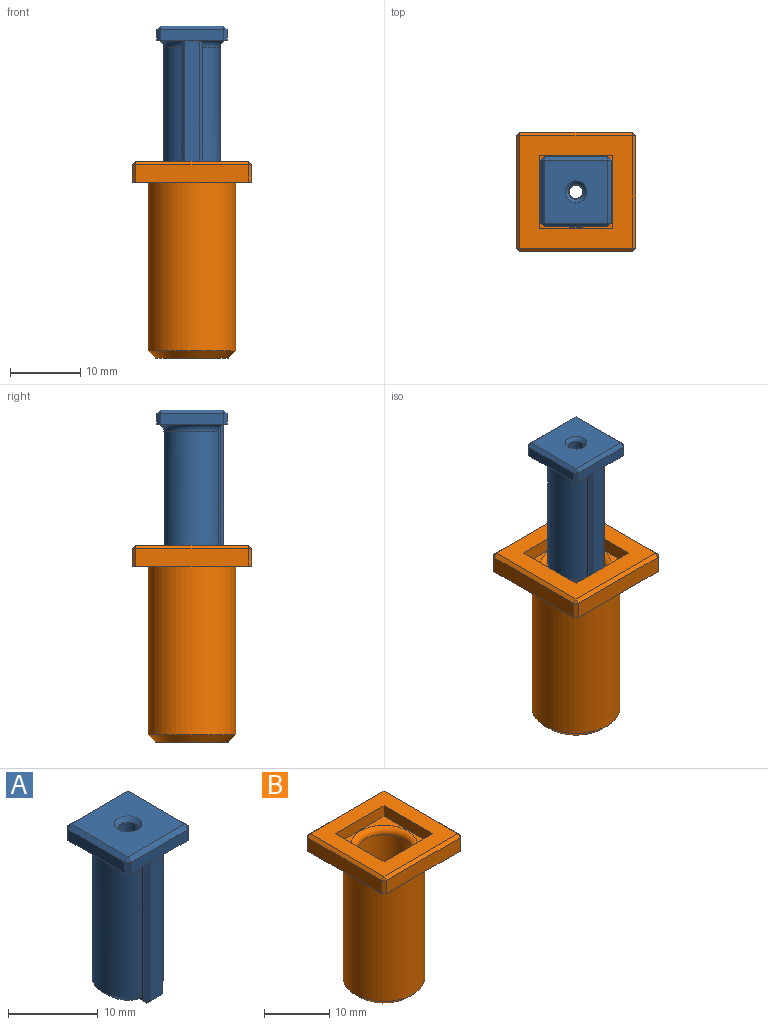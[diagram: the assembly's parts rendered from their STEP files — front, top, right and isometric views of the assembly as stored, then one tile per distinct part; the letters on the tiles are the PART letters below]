
ASSEMBLY  parts=2 mates=1
PART A: 39 faces, bbox 10.9x10.9x22 mm
  f0: plane 5x5mm, normal (0,0,-1), area 5.2mm2, adj f4,f7,f24,f30
  f1: plane 5x5mm, normal (0,0,-1), area 5.2mm2, adj f4,f5,f23,f30
  f2: plane 5x5mm, normal (0,0,-1), area 5.2mm2, adj f5,f6,f17,f30
  f3: plane 5x5mm, normal (0,0,-1), area 5.2mm2, adj f6,f7,f18,f30
  f4: plane 9x1.5mm, normal (1,0,0), area 13.5mm2, adj f0,f1,f23,f24,f28
  f5: plane 9x1.5mm, normal (0,1,0), area 13.5mm2, adj f1,f2,f17,f22,f23
  f6: plane 9x1.5mm, normal (-1,0,0), area 13.5mm2, adj f2,f3,f17,f18,f19
  f7: plane 9x1.5mm, normal (0,-1,0), area 13.5mm2, adj f0,f3,f18,f24,f25
  f8: plane 9x9mm, normal (0,0,1), area 73.5mm2, adj f19,f22,f25,f28,f29
  f9: cylinder r=4mm len=18mm, axis (0,0,1), area 397mm2, adj f10,f12,f30,f31
  f10: plane 19.23x0.89mm, normal (1,0,0), area 5.7mm2, adj f9,f30,f31,f35,f38
  f11: plane 19.42x2mm, normal (0,-1,0), area 38.8mm2, adj f30,f33,f36,f38
  f12: plane 19.23x0.89mm, normal (-1,0,0), area 5.7mm2, adj f9,f30,f31,f32,f33
  f13: plane 7x6mm, normal (0,0,-1), area 27.6mm2, adj f14,f31,f32,f35,f36
  f14: cylinder r=0.95mm len=7mm, axis (0,0,1), area 41.8mm2, adj f13,f16
  f15: cylinder r=1.05mm len=14.5mm, axis (0,0,1), area 95.7mm2, adj f16,f29
  f16: plane 2.1x2.1mm, normal (0,0,1), area 0.6mm2, adj f14,f15
  f17: plane 1.5x0.5mm, normal (-0.71,0.71,0), area 1.1mm2, adj f2,f5,f6,f20
  f18: plane 1.5x0.5mm, normal (-0.71,-0.71,0), area 1.1mm2, adj f3,f6,f7,f21
  f19: plane 9x0.5mm, normal (-0.71,0,0.71), area 6.4mm2, adj f6,f8,f20,f21
  f20: plane 0.5x0.5mm, normal (-0.58,0.58,0.58), area 0.2mm2, adj f17,f19,f22
  f21: plane 0.5x0.5mm, normal (-0.58,-0.58,0.58), area 0.2mm2, adj f18,f19,f25
  f22: plane 9x0.5mm, normal (0,0.71,0.71), area 6.4mm2, adj f5,f8,f20,f26
  f23: plane 1.5x0.5mm, normal (0.71,0.71,0), area 1.1mm2, adj f1,f4,f5,f26
  f24: plane 1.5x0.5mm, normal (0.71,-0.71,0), area 1.1mm2, adj f0,f4,f7,f27
  f25: plane 9x0.5mm, normal (0,-0.71,0.71), area 6.4mm2, adj f7,f8,f21,f27
  f26: plane 0.5x0.5mm, normal (0.58,0.58,0.58), area 0.2mm2, adj f22,f23,f28
  f27: plane 0.5x0.5mm, normal (0.58,-0.58,0.58), area 0.2mm2, adj f24,f25,f28
  f28: plane 9x0.5mm, normal (0.71,0,0.71), area 6.4mm2, adj f4,f8,f26,f27
  f29: cone r=1.05mm half-angle=45deg, axis (0,0,1), area 5.8mm2, adj f8,f15
  f30: torus R=5mm, axis (0,0,1), area 39.9mm2, adj f0,f1,f2,f3,f9,f10,f11,f12
  f31: cone r=3mm half-angle=45deg, axis (0,0,1), area 27.1mm2, adj f9,f10,f12,f13,f32,f35
  f32: plane 1.19x0.52mm, normal (-0.71,0,-0.71), area 0.7mm2, adj f12,f13,f31,f34
  f33: plane 19.44x0.51mm, normal (-0.71,-0.71,0), area 13.7mm2, adj f11,f12,f30,f34
  f34: plane 0.5x0.5mm, normal (-0.58,-0.58,-0.58), area 0.2mm2, adj f32,f33,f36
  f35: plane 1.19x0.52mm, normal (0.71,0,-0.71), area 0.7mm2, adj f10,f13,f31,f37
  f36: plane 2x0.5mm, normal (0,-0.71,-0.71), area 1.4mm2, adj f11,f13,f34,f37
  f37: plane 0.5x0.5mm, normal (0.58,-0.58,-0.58), area 0.2mm2, adj f35,f36,f38
  f38: plane 19.44x0.51mm, normal (0.71,-0.71,0), area 13.7mm2, adj f10,f11,f30,f37
PART B: 38 faces, bbox 21x21x32 mm
  f0: torus R=5.05mm, axis (0,0,1), area 199.4mm2, adj f13,f16
  f1: plane 16x16mm, normal (0,0,1), area 145.7mm2, adj f9,f10,f11,f12,f27,f30,f33,f36
  f2: plane 16x2.5mm, normal (0,-1,0), area 40mm2, adj f6,f25,f30,f31
  f3: plane 16x2.5mm, normal (1,0,0), area 40mm2, adj f6,f25,f26,f27
  f4: plane 16x2.5mm, normal (0,1,0), area 40mm2, adj f6,f26,f32,f33
  f5: plane 16x2.5mm, normal (-1,0,0), area 40mm2, adj f6,f31,f32,f36
  f6: plane 17x17mm, normal (0,0,-1), area 165.8mm2, adj f2,f3,f4,f5,f7,f25,f26,f31
  f7: cylinder r=6.25mm len=24mm, axis (0,0,1), area 942.5mm2, adj f6,f37
  f8: plane 10.5x10.5mm, normal (0,0,-1), area 32.8mm2, adj f14,f15,f16,f17,f19,f22,f37
  f9: plane 10.5x2mm, normal (0,1,0), area 21mm2, adj f1,f10,f12,f13
  f10: plane 10.5x2mm, normal (-1,0,0), area 21mm2, adj f1,f9,f11,f13
  f11: plane 10.5x2mm, normal (0,-1,0), area 21mm2, adj f1,f10,f12,f13
  f12: plane 10.5x2mm, normal (1,0,0), area 21mm2, adj f1,f9,f11,f13
  f13: plane 14.5x14.5mm, normal (0,0,1), area 30.2mm2, adj f0,f9,f10,f11,f12,f16,f18
  f14: cylinder r=4.05mm len=25mm, axis (0,0,-1), area 542.9mm2, adj f8,f18,f19,f22
  f15: plane 25.56x0.63mm, normal (-1,0,0), area 15.8mm2, adj f8,f16,f22,f23
  f16: plane 30x8mm, normal (0,1,0), area 80.6mm2, adj f0,f8,f13,f15,f17,f20,f24
  f17: plane 25.57x0.64mm, normal (1,0,0), area 15.8mm2, adj f8,f16,f19,f21
  f18: torus R=5.05mm, axis (0,0,1), area 37.6mm2, adj f13,f14,f21,f23
  f19: plane 25x0.4mm, normal (0.85,0.53,0), area 11.8mm2, adj f8,f14,f17,f21
  f20: plane 0.45x0.45mm, normal (0.71,0,0.71), area 0mm2, adj f16,f21
  f21: bspline ~1.01x1mm, area 0.7mm2, adj f17,f18,f19,f20
  f22: plane 25x0.4mm, normal (-0.85,0.53,0), area 11.8mm2, adj f8,f14,f15,f23
  f23: bspline ~1.23x1.04mm, area 0.7mm2, adj f15,f18,f22,f24
  f24: plane 0.45x0.45mm, normal (-0.71,0,0.71), area 0mm2, adj f16,f23
  f25: plane 2.5x0.5mm, normal (0.71,-0.71,0), area 1.8mm2, adj f2,f3,f6,f28
  f26: plane 2.5x0.5mm, normal (0.71,0.71,0), area 1.8mm2, adj f3,f4,f6,f29
  f27: plane 16x0.5mm, normal (0.71,0,0.71), area 11.3mm2, adj f1,f3,f28,f29
  f28: plane 0.5x0.5mm, normal (0.58,-0.58,0.58), area 0.2mm2, adj f25,f27,f30
  f29: plane 0.5x0.5mm, normal (0.58,0.58,0.58), area 0.2mm2, adj f26,f27,f33
  f30: plane 16x0.5mm, normal (0,-0.71,0.71), area 11.3mm2, adj f1,f2,f28,f34
  f31: plane 2.5x0.5mm, normal (-0.71,-0.71,0), area 1.8mm2, adj f2,f5,f6,f34
  f32: plane 2.5x0.5mm, normal (-0.71,0.71,0), area 1.8mm2, adj f4,f5,f6,f35
  f33: plane 16x0.5mm, normal (0,0.71,0.71), area 11.3mm2, adj f1,f4,f29,f35
  f34: plane 0.5x0.5mm, normal (-0.58,-0.58,0.58), area 0.2mm2, adj f30,f31,f36
  f35: plane 0.5x0.5mm, normal (-0.58,0.58,0.58), area 0.2mm2, adj f32,f33,f36
  f36: plane 16x0.5mm, normal (-0.71,0,0.71), area 11.3mm2, adj f1,f5,f34,f35
  f37: cone r=5.25mm half-angle=45deg, axis (0,0,1), area 51.1mm2, adj f7,f8
PLACE A t=(-5.57,-25.67,15.95)mm
PLACE B t=(-5.57,-25.67,-4.25)mm
MATE slider B.f0 <-> A.f9  axis (0,0,-1) through (-5.57,-25.67,-4.25)mm
